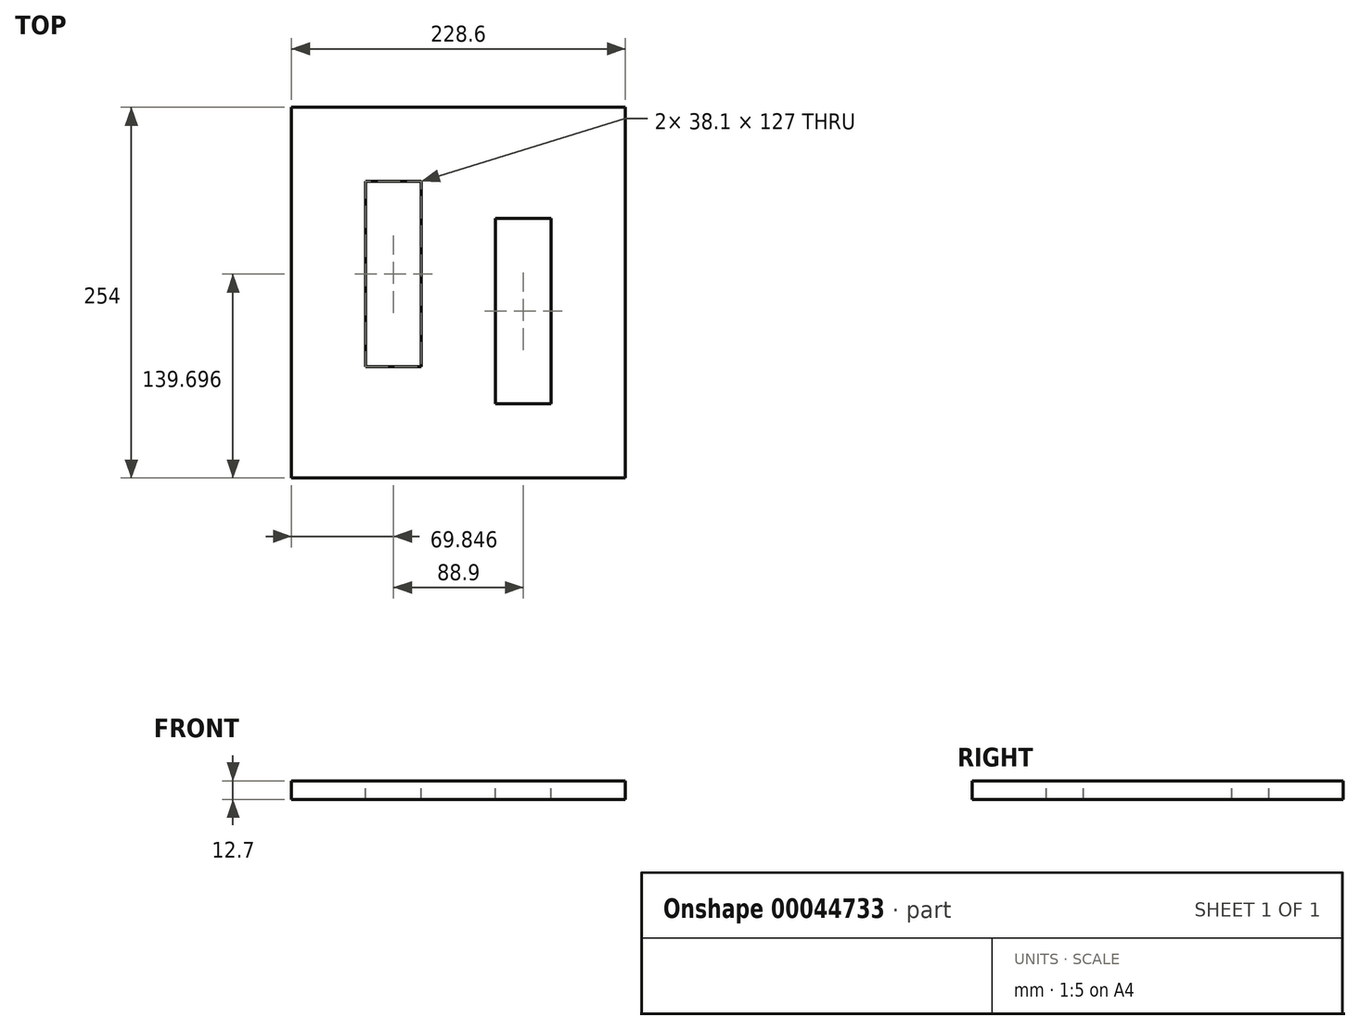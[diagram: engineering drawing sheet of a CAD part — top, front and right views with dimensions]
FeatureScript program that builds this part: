
annotation { "Feature Type Name" : "Feature", "Feature Type Description" : "" }
export const myFeature = defineFeature(function(context is Context, id is Id, definition is map)
    precondition{}
    {
        {
            var Q0;
            Q0=qCreatedBy(makeId("Top.planeOp"),FACE);
            var sketch = newSketch(context, id + "F0", { "sketchPlane" : qUnion([Q0])});
            skLineSegment(sketch, "E0.bottom", {"start": v(-108.73, -87.24) * mm, "end": v(119.87, -87.24) * mm});
            skLineSegment(sketch, "E0.top", {"start": v(-108.73, 166.76) * mm, "end": v(119.87, 166.76) * mm});
            skLineSegment(sketch, "E0.left", {"start": v(-108.73, -87.24) * mm, "end": v(-108.73, 166.76) * mm});
            skLineSegment(sketch, "E0.right", {"start": v(119.87, -87.24) * mm, "end": v(119.87, 166.76) * mm});
            skSolve(sketch);
        }
        {
            var Q0;
            Q0 = qSketchRegion(id + "F0", true);
            var Q1;
            Q1=sQuery(id+"F0.wireOp",EDGE,"E0.bottom");
            var Q2;
            Q2=sQuery(id+"F0.wireOp",EDGE,"E0.right");
            var Q3;
            Q3=sQuery(id+"F0.wireOp",EDGE,"E0.left");
            var Q4;
            Q4=sQuery(id+"F0.wireOp",EDGE,"E0.top");
            extrude(context, id + "F1", {"entities" : qUnion([Q0]), "surfaceEntities" : qUnion([Q1, Q2, Q3, Q4]), "depth" : 12.7 * mm});
        }
        {
            var Q0;
            Q0=makeQuery(id+"F1.opExtrude","CAP_FACE",FACE,{"disambiguationData":[OSD([sQuery(id+"F0.wireOp",EDGE,"E0.bottom"),sQuery(id+"F0.wireOp",EDGE,"E0.top"),sQuery(id+"F0.wireOp",EDGE,"E0.left"),sQuery(id+"F0.wireOp",EDGE,"E0.right")])],"isStart":false});
            var sketch = newSketch(context, id + "F2", { "sketchPlane" : qUnion([Q0])});
            skLineSegment(sketch, "E1.rect.bottom", {"start": v(-19.83, -11.04) * mm, "end": v(-57.93, -11.04) * mm});
            skLineSegment(sketch, "E1.rect.top", {"start": v(-19.83, 115.96) * mm, "end": v(-57.93, 115.96) * mm});
            skLineSegment(sketch, "E1.rect.left", {"start": v(-19.83, -11.04) * mm, "end": v(-19.83, 115.96) * mm});
            skLineSegment(sketch, "E1.rect.right", {"start": v(-57.93, -11.04) * mm, "end": v(-57.93, 115.96) * mm});
            skPoint(sketch, "E1.rect.middle", {"position": v(-38.88, 52.46) * mm});
            skLineSegment(sketch, "E2.rect.bottom", {"start": v(69.07, -36.44) * mm, "end": v(30.97, -36.44) * mm});
            skLineSegment(sketch, "E2.rect.top", {"start": v(69.07, 90.56) * mm, "end": v(30.97, 90.56) * mm});
            skLineSegment(sketch, "E2.rect.left", {"start": v(69.07, -36.44) * mm, "end": v(69.07, 90.56) * mm});
            skLineSegment(sketch, "E2.rect.right", {"start": v(30.97, -36.44) * mm, "end": v(30.97, 90.56) * mm});
            skPoint(sketch, "E2.rect.middle", {"position": v(50.02, 27.06) * mm});
            skSolve(sketch);
        }
        {
            var Q0;
            Q0=makeQuery(id+"F2.imprint","IMPRINT",FACE,{"disambiguationData":[TD([[makeQuery(id+"F2.imprint","IMPRINT",EDGE,{"derivedFrom":sQuery(id+"F2.wireOp",EDGE,"E1.rect.bottom")}),-1.0]])]});
            var Q1;
            Q1=makeQuery(id+"F2.imprint","IMPRINT",FACE,{"disambiguationData":[TD([[makeQuery(id+"F2.imprint","IMPRINT",EDGE,{"derivedFrom":sQuery(id+"F2.wireOp",EDGE,"E2.rect.bottom")}),-1.0]])]});
            extrude(context, id + "F3", {"entities" : qUnion([Q0, Q1]), "operationType" : NewBodyOperationType.REMOVE, "oppositeDirection" : true, "depth" : 12.7 * mm});
        }
    });
